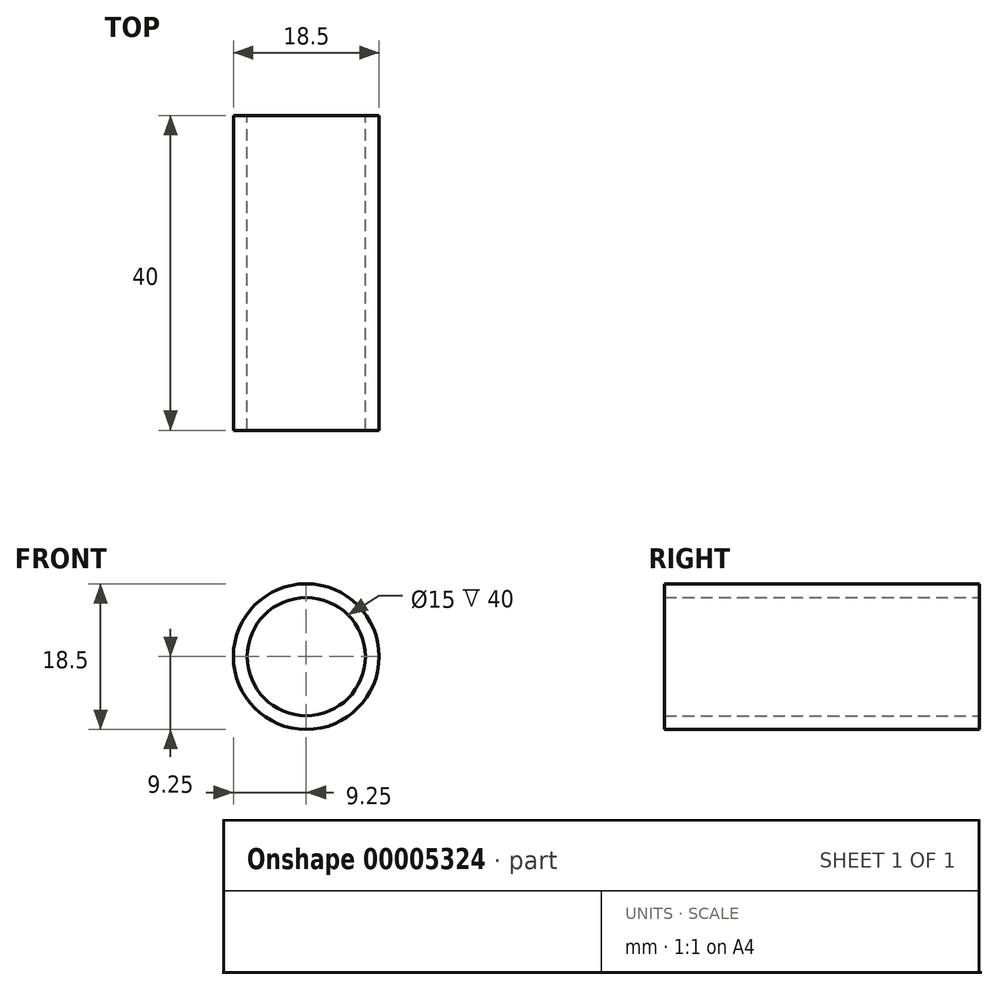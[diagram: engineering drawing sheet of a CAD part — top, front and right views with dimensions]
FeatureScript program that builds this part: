
annotation { "Feature Type Name" : "Feature", "Feature Type Description" : "" }
export const myFeature = defineFeature(function(context is Context, id is Id, definition is map)
    precondition{}
    {
        {
            var Q0;
            Q0=qCreatedBy(makeId("Front.planeOp"),FACE);
            var sketch = newSketch(context, id + "F0", { "sketchPlane" : qUnion([Q0])});
            skCircle(sketch, "E0", {"center": v(0, 0) * mm, "radius": 7.5 * mm});
            skCircle(sketch, "E1", {"center": v(0, 0) * mm, "radius": 9.25 * mm});
            skSolve(sketch);
        }
        {
            var Q0;
            Q0=makeQuery(id+"F0.imprint","IMPRINT",FACE,{"disambiguationData":[TD([[makeQuery(id+"F0.imprint","IMPRINT",EDGE,{"derivedFrom":sQuery(id+"F0.wireOp",EDGE,"E0")}),-1.0]])]});
            extrude(context, id + "F1", {"entities" : qUnion([Q0]), "depth" : 40 * mm});
        }
    });
